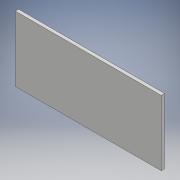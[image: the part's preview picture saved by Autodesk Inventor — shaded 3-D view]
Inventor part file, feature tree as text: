
AUTODESK INVENTOR PART (.ipt)
format: ipt  version: 2018 (Build 220112000, 112)  size: 90,112 bytes
history: native  units: mm
features: extrude x1, sketch x1
ambient origin geometry x8: Origin, YZ Plane, XZ Plane, XY Plane, X Axis, Y Axis, Z Axis, Center Point
bodies: 实体1 (feature_tree)
feature tree (2):
  extrude  "拉伸1"  Depth=1.5mm TaperAngle=0.0deg
  sketch  "草图1"  dims[d0=30.0mm d1=1.5mm d2=0.0mm d3=67.0mm]
